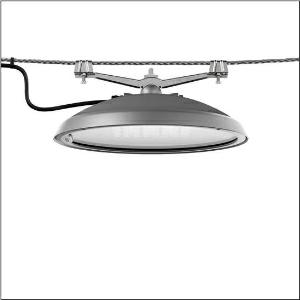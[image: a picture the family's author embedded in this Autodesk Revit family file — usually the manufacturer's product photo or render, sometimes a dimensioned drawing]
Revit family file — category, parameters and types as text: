
# Revit family: dl_r__50_iq_mini___st0_8s_5xa248v41f08ge_d665
name_source: partatom
category: Lighting Fixtures
units: mm (PartAtom-declared; Revit-internal decimal feet)

## family parameters
Cut with Voids When Loaded = No
Host = Face
Light Source = No
Part Type = Normal
Room Calculation Point = No
Round Connector Dimension = Use Diameter
Shared = No

## types (1)
- --- (1 x LED, 5190 lm, 31.2 W, 4000K)
    Apparent Load = 31 VA
    CIE Flux Codes = 38 75 97 100 100
    Color Rendering = 70
    Color Temperature = 4000K
    Default Elevation = 1800 mm
    Description = DL® 50 iQ mini, catenary luminaire, primary light control with lens, of PMMA, primary optical cover: cover, of toughened safety glass, transparent, light distribution: ST0.8s, light emission: direct distribution, primary light characteristic: symmetric, installation type: suspended mounting, LED, High Power LED, rated luminous flux: 5.190lm, luminous efficacy: 166lm/W, light colour: 740, colour temperature: 4000K, control: optimised constant luminous flux control (CLO 2.0), Desk-Remote (wireless, voltage-free reading and setting of iQ features in the workshop via application-optimized NFC function/RFID function), Light-Fading, Smart-Wire, Night-Set, Lumen-Switch, Temp-Guard, Auto-Match, Street-Remote, mains connection: 230..240V, AC, 50/60Hz, start of lifetime: 31W, end of service life: 32W, reduction: 15W, luminaire housing, of diecast aluminium, powder-coated, Siteco® metallic grey (DB 702S), diameter: 500mm, height: 115mm, protection rating (complete): IP66, insulation class (complete): insulation class II (safety insulation), certification: CE, ENEC, VDE, impact resistance: IK08, permissible operating ambient temperature for outdoor applications: -25..+40°C, standard-compliant lighting for roads and squares, packaging unit: 1 piece

Light Distribution: ST0.8s
    Height = 124 mm  [stored 0.406824 ft]
    Lamp = 1 x LED
    Lamp Light Flux = 5190 lm
    Lamp Power = 31.2 W
    Lamp count = 1
    Length = 500 mm
    Luminous efficacy = 166 lm/W
    Manufacturer = Siteco
    ModVariant = No
    Model = 5XA248V41F08GE
    Number of Poles = 1
    OnlyDefault = Yes
    Power Factor = 1
    Product Name = DL® 50 iQ mini | ST0.8s
    Product group = catenary luminaire
    ProductGroupID = 6300
    Protection Class = Protection class II
    Protection Degree = IP 66
    RLX_Detail_Level = 1
    RLX_Emergency_Light_Flux = 0 lm
    RLX_Emergency_Type = 0
    RLX_Emergency_Type_DB = No
    RlxData = <blob elided: 123541 chars, md5=83ce232d>
    Socket = socket
    Standby Power = 0 W
    System Light Flux = 5190 lm
    System Power = 31 W
    Type Comments = factory setting: luminous flux: 100 % | dim-lin: 254 | 325 mA
    Type Image = l_1242791.jpg
    URL = http://relux.com
    VarID = @adj_090465
    Voltage = 0 V
    Weight = 0.00 kg
    Width = 0 mm  [stored 0 ft]

note: [stored X ft] marks values corroborated as IEEE doubles in the binary element streams (Revit-internal decimal feet)

## geometry (parser evidence)
native form markers: Blend x4, Sweep x13
no freeform markers — native parametric forms only
